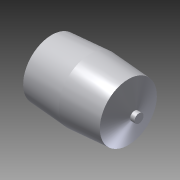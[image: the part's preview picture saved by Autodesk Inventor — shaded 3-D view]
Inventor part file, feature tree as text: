
AUTODESK INVENTOR PART (.ipt)
format: ipt  version: 2014 (Build 180170000, 170)  size: 102,400 bytes
history: native  units: in
note: dims shown in document units (in); Inventor stores cm internally (conversion verified against a paired STEP export)
features: revolve x1, sketch x1
ambient origin geometry x8: Origin, YZ Plane, XZ Plane, XY Plane, X Axis, Y Axis, Z Axis, Center Point
bodies: Solid1 (feature_tree)
feature tree (2):
  revolve  "Revolution1"  [1 undecoded]
  sketch  "Sketch1"  dims[d0=0.55in d1=0.175in d2=0.025in d3=0.16in d4=0.43in d5=0.5in d6=90.0deg]
note: 1 required parameter value undecoded (feature->parameter linkage not recoverable at this tier; creation-order binding heuristic only, values carry confidence <= 0.55)
